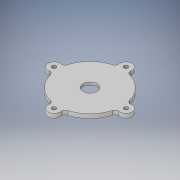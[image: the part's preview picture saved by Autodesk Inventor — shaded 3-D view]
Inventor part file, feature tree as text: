
AUTODESK INVENTOR PART (.ipt)
format: ipt  version: 2019 (Build 230136000, 136)  size: 561,664 bytes
history: native  units: in
note: dims shown in document units (in); Inventor stores cm internally (conversion verified against a paired STEP export)
features: extrude x5, sketch x5, fillet x1
ambient origin geometry x8: Origin, YZ Plane, XZ Plane, XY Plane, X Axis, Y Axis, Z Axis, Center Point
bodies: Solid1 (feature_tree)
feature tree (11):
  extrude  "Extrusion1"  Depth=0.15in TaperAngle=0.0deg
  extrude  "Extrusion2"  Depth=0.1in
  extrude  "Extrusion3"  Depth=0.125in
  extrude  "Extrusion4"  Depth=0.15in
  fillet  "Fillet1"  Radius=0.15in
  extrude  "Extrusion5"  Depth=0.15in TaperAngle=0.0deg
  sketch  "Sketch1"  dims[d0=0.15in d1=0.0in d2=0.15in d3=0.0in]
  sketch  "Sketch2"  dims[d4=0.1in d5=0.0in d6=0.5in]
  sketch  "Sketch3"  dims[d7=0.1in d8=0.0in d9=0.125in]
  sketch  "Sketch4"  dims[d10=0.15in d11=0.15in d12=0.15in]
  sketch  "Sketch5"  dims[d13=0.15in d14=0.2in d15=0.0in]
